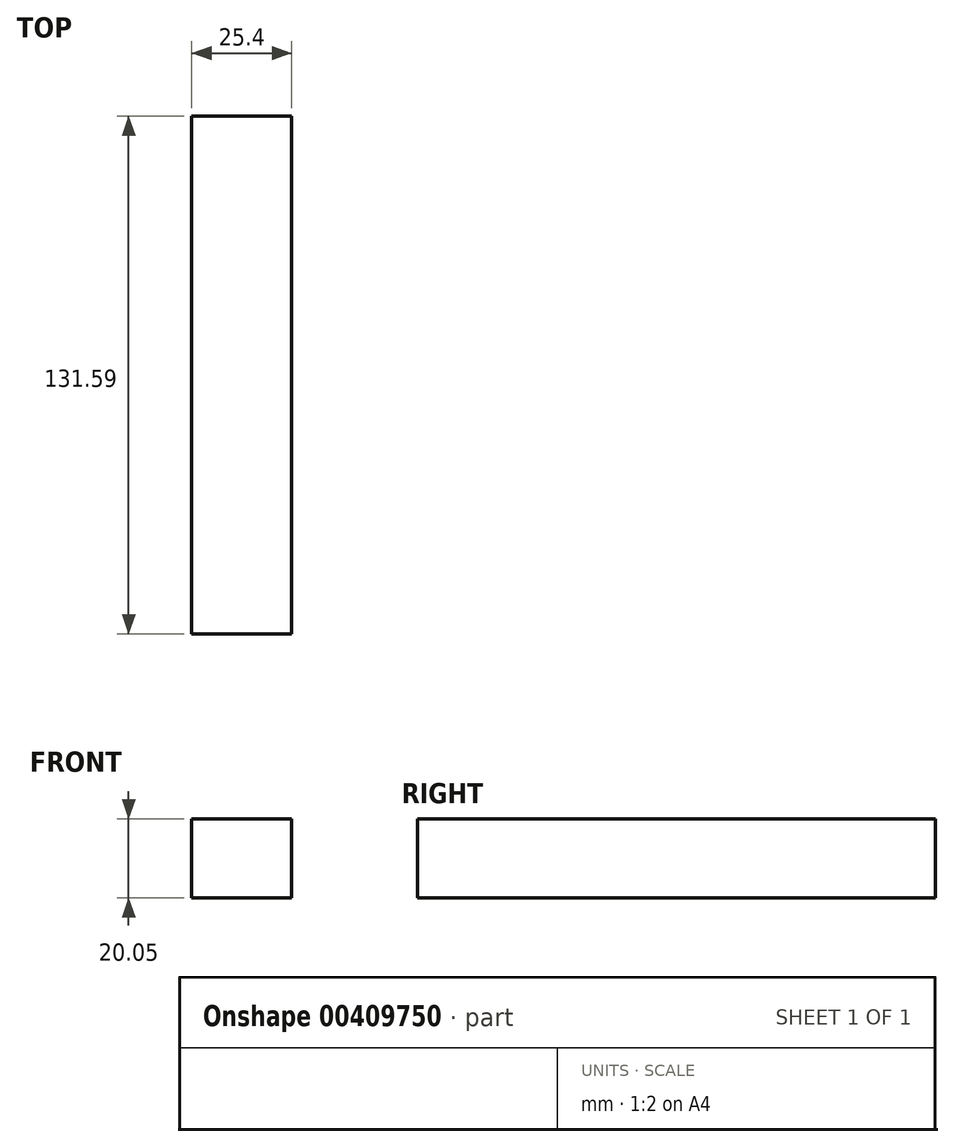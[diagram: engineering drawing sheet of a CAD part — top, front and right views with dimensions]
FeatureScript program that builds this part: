
annotation { "Feature Type Name" : "Feature", "Feature Type Description" : "" }
export const myFeature = defineFeature(function(context is Context, id is Id, definition is map)
    precondition{}
    {
        {
            var Q0;
            Q0=qCreatedBy(makeId("Right.planeOp"),FACE);
            var sketch = newSketch(context, id + "F0", { "sketchPlane" : qUnion([Q0])});
            skLineSegment(sketch, "E0.bottom", {"start": v(45.11, 0) * mm, "end": v(-86.48, 0) * mm});
            skLineSegment(sketch, "E0.top", {"start": v(45.11, -20.05) * mm, "end": v(-86.48, -20.05) * mm});
            skLineSegment(sketch, "E0.left", {"start": v(45.11, 0) * mm, "end": v(45.11, -20.05) * mm});
            skLineSegment(sketch, "E0.right", {"start": v(-86.48, 0) * mm, "end": v(-86.48, -20.05) * mm});
            skSolve(sketch);
        }
        {
            var Q0;
            Q0=makeQuery(id+"F0.imprint","IMPRINT",FACE,{"disambiguationData":[TD([[makeQuery(id+"F0.imprint","IMPRINT",EDGE,{"derivedFrom":sQuery(id+"F0.wireOp",EDGE,"E0.bottom")}),1.0]])]});
            extrude(context, id + "F1", {"entities" : qUnion([Q0]), "depth" : 25.4 * mm});
        }
    });
